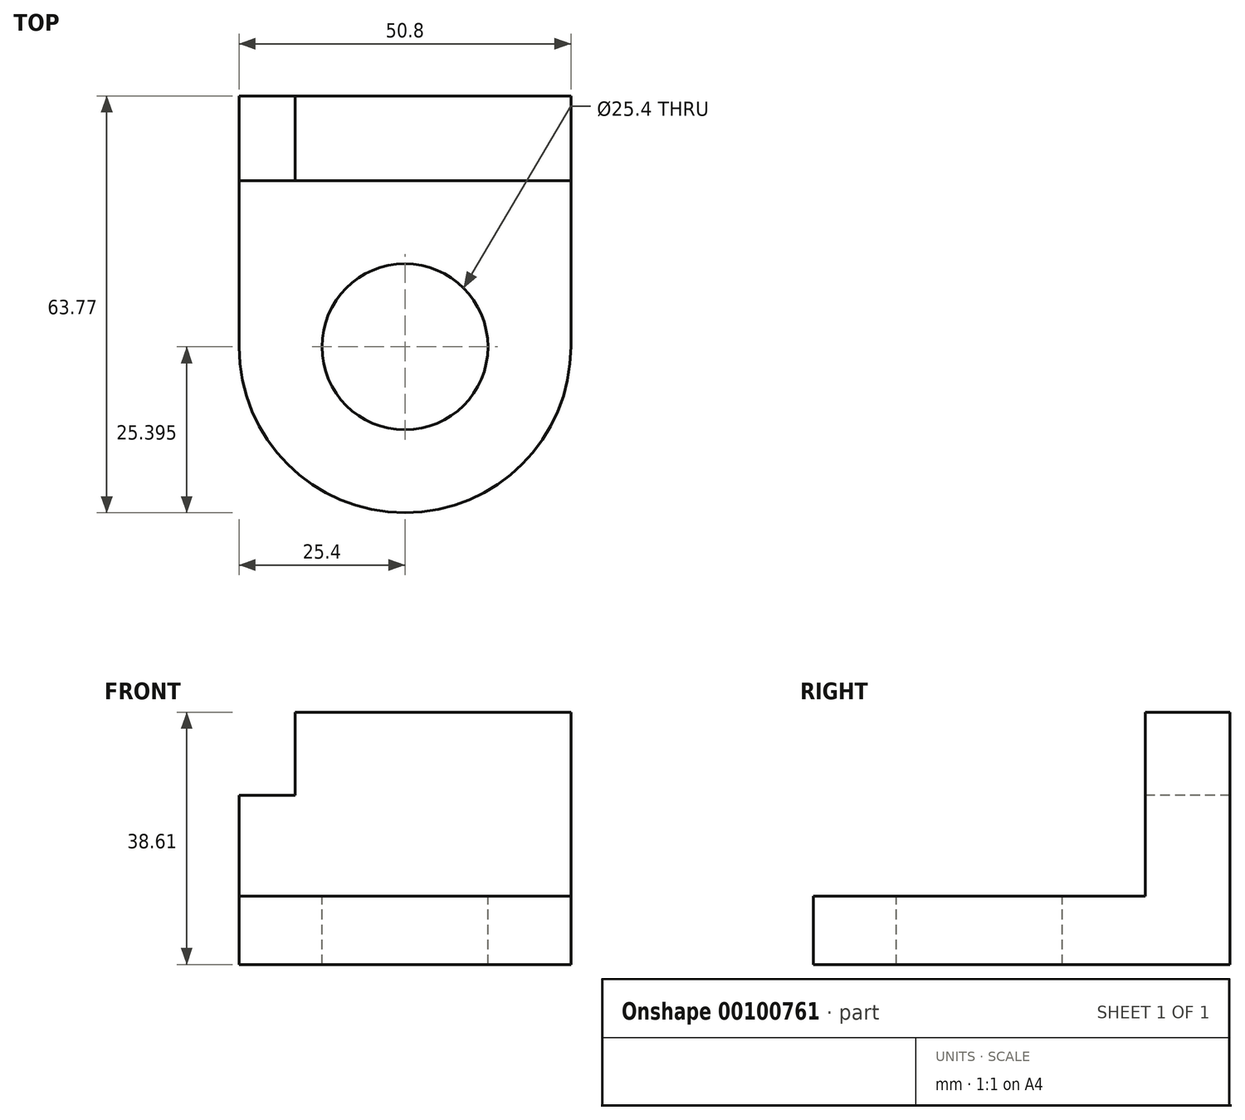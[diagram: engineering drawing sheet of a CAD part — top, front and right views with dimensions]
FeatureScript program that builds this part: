
annotation { "Feature Type Name" : "Feature", "Feature Type Description" : "" }
export const myFeature = defineFeature(function(context is Context, id is Id, definition is map)
    precondition{}
    {
        {
            var Q0;
            Q0=qCreatedBy(makeId("Right.planeOp"),FACE);
            var sketch = newSketch(context, id + "F0", { "sketchPlane" : qUnion([Q0])});
            skLineSegment(sketch, "E0.bottom", {"start": v(29.17, -10.43) * mm, "end": v(42.14, -10.43) * mm});
            skLineSegment(sketch, "E0.top", {"start": v(29.17, 15.48) * mm, "end": v(42.14, 15.48) * mm});
            skLineSegment(sketch, "E0.left", {"start": v(29.17, -10.43) * mm, "end": v(29.17, 15.48) * mm});
            skLineSegment(sketch, "E0.right", {"start": v(42.14, -10.43) * mm, "end": v(42.14, 15.48) * mm});
            skSolve(sketch);
        }
        {
            var Q0;
            Q0 = qSketchRegion(id + "F0", true);
            extrude(context, id + "F1", {"entities" : qUnion([Q0]), "endBound" : BoundingType.SYMMETRIC, "depth" : 50.8 * mm});
        }
        {
            var Q0;
            Q0=makeQuery(id+"F1.opExtrude","SWEPT_FACE",FACE,{"disambiguationData":[OSD([sQuery(id+"F0.wireOp",EDGE,"E0.top")])]});
            var sketch = newSketch(context, id + "F2", { "sketchPlane" : qUnion([Q0])});
            skLineSegment(sketch, "E1.bottom", {"start": v(-16.82, 42.14) * mm, "end": v(25.4, 42.14) * mm});
            skLineSegment(sketch, "E1.top", {"start": v(-16.82, 29.17) * mm, "end": v(25.4, 29.17) * mm});
            skLineSegment(sketch, "E1.left", {"start": v(-16.82, 42.14) * mm, "end": v(-16.82, 29.17) * mm});
            skLineSegment(sketch, "E1.right", {"start": v(25.4, 42.14) * mm, "end": v(25.4, 29.17) * mm});
            skSolve(sketch);
        }
        {
            var Q0;
            Q0=makeQuery(id+"F2.imprint","IMPRINT",FACE,{"disambiguationData":[TD([[makeQuery(id+"F2.imprint","IMPRINT",EDGE,{"derivedFrom":sQuery(id+"F2.wireOp",EDGE,"E1.bottom")}),1.0]])]});
            extrude(context, id + "F3", {"entities" : qUnion([Q0]), "operationType" : NewBodyOperationType.ADD, "depth" : 12.7 * mm});
        }
        {
            var Q0;
            Q0=makeQuery(id+"F3.boolean.opBoolean","MERGE",FACE,{"derivedFrom":[makeQuery(id+"F1.opExtrude","SWEPT_FACE",FACE,{"disambiguationData":[OSD([sQuery(id+"F0.wireOp",EDGE,"E0.left")])]}),makeQuery(id+"F3.opExtrude","SWEPT_FACE",FACE,{"disambiguationData":[OSD([sQuery(id+"F2.wireOp",EDGE,"E1.top")])]})]});
            var sketch = newSketch(context, id + "F4", { "sketchPlane" : qUnion([Q0])});
            skLineSegment(sketch, "E2.bottom", {"start": v(25.4, -10.43) * mm, "end": v(-25.4, -10.43) * mm});
            skLineSegment(sketch, "E2.top", {"start": v(25.4, 0) * mm, "end": v(-25.4, 0) * mm});
            skLineSegment(sketch, "E2.left", {"start": v(25.4, -10.43) * mm, "end": v(25.4, 0) * mm});
            skLineSegment(sketch, "E2.right", {"start": v(-25.4, -10.43) * mm, "end": v(-25.4, 0) * mm});
            skSolve(sketch);
        }
        {
            var Q0;
            Q0 = qSketchRegion(id + "F4", true);
            extrude(context, id + "F5", {"entities" : qUnion([Q0]), "operationType" : NewBodyOperationType.ADD, "depth" : 50.8 * mm});
        }
        {
            var Q0;
            Q0=makeQuery(id+"F5.opExtrude","SWEPT_FACE",FACE,{"disambiguationData":[OSD([sQuery(id+"F4.wireOp",EDGE,"E2.top")])]});
            var sketch = newSketch(context, id + "F6", { "sketchPlane" : qUnion([Q0])});
            skCircle(sketch, "E3", {"center": v(0, 3.77) * mm, "radius": 12.7 * mm});
            skSolve(sketch);
        }
        {
            var Q0;
            Q0=makeQuery(id+"F6.imprint","IMPRINT",FACE,{"disambiguationData":[TD([[makeQuery(id+"F6.imprint","IMPRINT",EDGE,{"derivedFrom":sQuery(id+"F6.wireOp",EDGE,"E3")}),1.0]])]});
            extrude(context, id + "F7", {"entities" : qUnion([Q0]), "operationType" : NewBodyOperationType.REMOVE, "endBound" : BoundingType.THROUGH_ALL, "oppositeDirection" : true, "depth" : 25.4 * mm});
        }
        {
            var Q0;
            Q0=makeQuery(id+"F5.opExtrude","CAP_EDGE",EDGE,{"disambiguationData":[OSD([sQuery(id+"F4.wireOp",EDGE,"E2.right")])],"isStart":false});
            fillet(context, id + "F8", {"entities" : qUnion([Q0]), "radius" : 25.4 * mm, "tangentPropagation" : true, "allowEdgeOverflow" : false});
        }
        {
            var Q0;
            Q0=makeQuery(id+"F5.opExtrude","CAP_EDGE",EDGE,{"disambiguationData":[OSD([sQuery(id+"F4.wireOp",EDGE,"E2.left")])],"isStart":false});
            fillet(context, id + "F9", {"entities" : qUnion([Q0]), "radius" : 25.4 * mm, "tangentPropagation" : true, "allowEdgeOverflow" : false});
        }
    });
